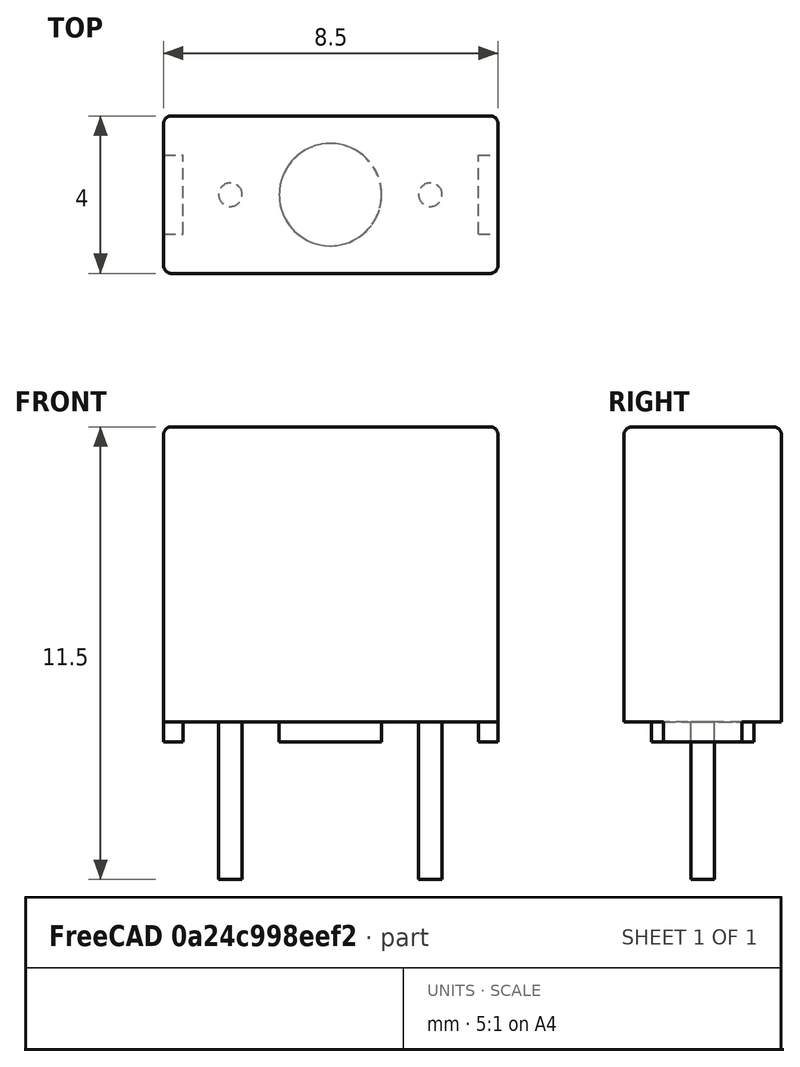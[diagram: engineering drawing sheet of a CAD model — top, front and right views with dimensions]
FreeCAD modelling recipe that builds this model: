
FCSTD DOCUMENT
Label: FUSE_TE5
Comment: Littelfuse TE5 392
objects: Part::Box×4, Part::Cylinder×3, Part::MultiFuse×2, Part::Cut×1, Part::Fillet×1
note: 11 computed .brp shape members not serialized (recipe doc carries the construction recipe); baked Part::Feature solids carry a one-line shape summary decoded from their .brp

FEATURE [Part::Box] Box
  Height = 8
  Length = 8.5
  Placement = pos=(-4.24,-2,0) rot=(0,0,1;0rad)
  Width = 4
FEATURE [Part::Cylinder] Cylinder
  Angle = 360
  Height = 0.5
  Radius = 1.3
FEATURE [Part::Box] Box001
  Height = 0.5
  Length = 7.5
  Placement = pos=(-3.74,-3,0) rot=(0,0,1;0rad)
  Width = 6
FEATURE [Part::Box] Box001001
  Height = 0.5
  Length = 10.5
  Placement = pos=(-5.74,-4,0) rot=(0,0,1;0rad)
  Width = 3
FEATURE [Part::Box] Box001001001
  Height = 0.5
  Length = 10.5
  Placement = pos=(-5.74,1,0) rot=(0,0,1;0rad)
  Width = 3
FEATURE [Part::MultiFuse] Fusion
  Shapes = -> [Box001001,Box001001001,Box001]
FEATURE [Part::Cut] Cut
  Base = -> Box
  Tool = -> Fusion
FEATURE [Part::Cylinder] Cylinder001  label="PIN"
  Angle = 360
  Height = 4
  Placement = pos=(-2.54,0,-3.5) rot=(0,0,1;0rad)
  Radius = 0.3
FEATURE [Part::Cylinder] Cylinder001001  label="PIN001"
  Angle = 360
  Height = 4
  Placement = pos=(2.54,0,-3.5) rot=(0,0,1;0rad)
  Radius = 0.3
FEATURE [Part::Fillet] Fillet
  Base = -> Cut
  Edges = 8 edges r=0.2: [Edge1,Edge2,Edge3,Edge4,Edge6,Edge7,Edge14,Edge17]
FEATURE [Part::MultiFuse] Fusion001  label="FUSE_TE5"
  Shapes = -> [Fillet,Cylinder,Cylinder001,Cylinder001001]
